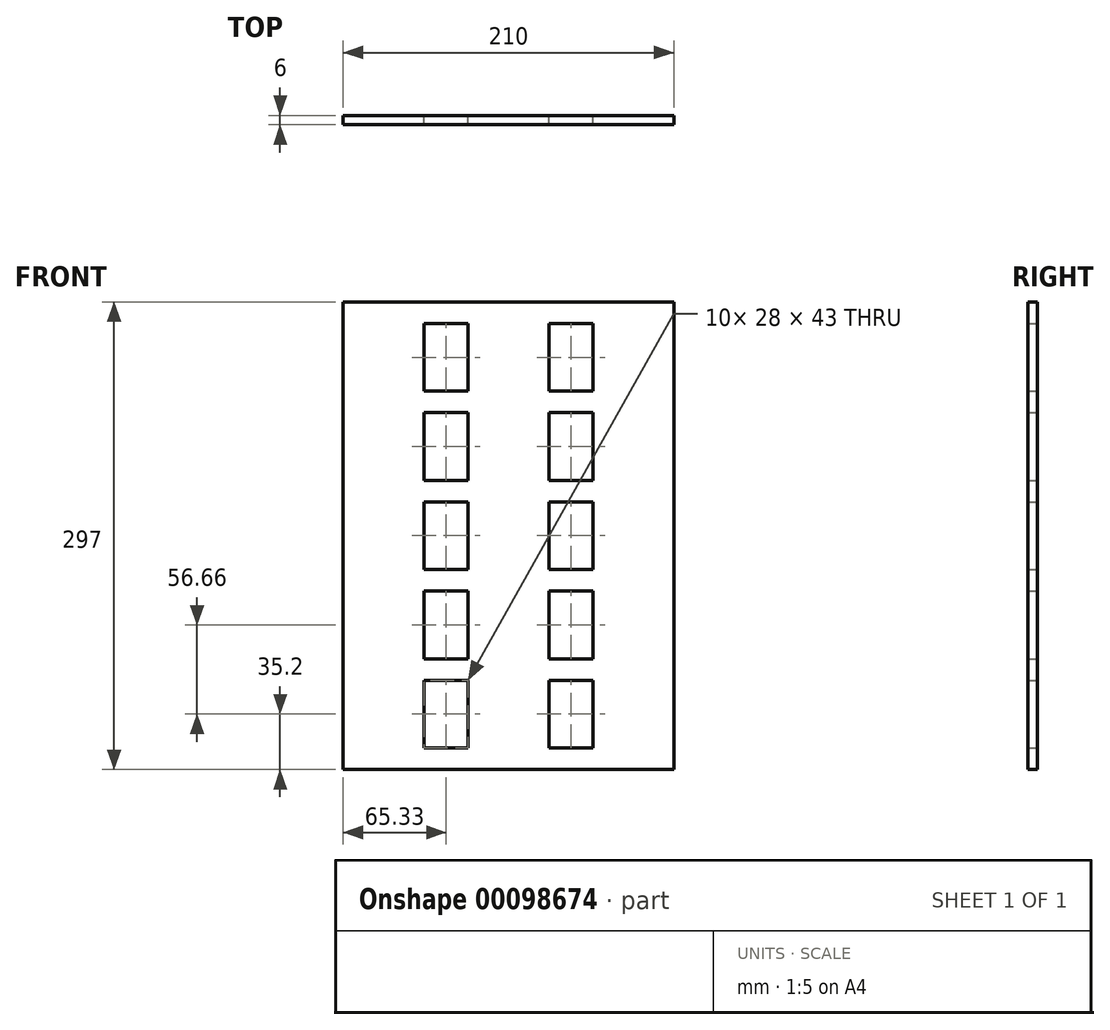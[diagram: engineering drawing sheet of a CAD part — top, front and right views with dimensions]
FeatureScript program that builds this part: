
annotation { "Feature Type Name" : "Feature", "Feature Type Description" : "" }
export const myFeature = defineFeature(function(context is Context, id is Id, definition is map)
    precondition{}
    {
        {
            var Q0;
            Q0=qCreatedBy(makeId("Front.planeOp"),FACE);
            var sketch = newSketch(context, id + "F0", { "sketchPlane" : qUnion([Q0])});
            skLineSegment(sketch, "E0.bottom", {"start": v(105, -148.5) * mm, "end": v(-105, -148.5) * mm});
            skLineSegment(sketch, "E0.top", {"start": v(105, 148.5) * mm, "end": v(-105, 148.5) * mm});
            skLineSegment(sketch, "E0.left", {"start": v(105, -148.5) * mm, "end": v(105, 148.5) * mm});
            skLineSegment(sketch, "E0.right", {"start": v(-105, -148.5) * mm, "end": v(-105, 148.5) * mm});
            skLineSegment(sketch, "E1.bottom", {"start": v(-25.67, 91.84) * mm, "end": v(-53.67, 91.84) * mm});
            skLineSegment(sketch, "E1.top", {"start": v(-25.67, 134.84) * mm, "end": v(-53.67, 134.84) * mm});
            skLineSegment(sketch, "E1.left", {"start": v(-25.67, 91.84) * mm, "end": v(-25.67, 134.84) * mm});
            skLineSegment(sketch, "E1.right", {"start": v(-53.67, 91.84) * mm, "end": v(-53.67, 134.84) * mm});
            skPoint(sketch, "E1.middle", {"position": v(-39.67, 113.34) * mm});
            skLineSegment(sketch, "E2.0.1.0", {"start": v(-25.67, 78.18) * mm, "end": v(-53.67, 78.18) * mm});
            skLineSegment(sketch, "E2.0.1.1", {"start": v(-53.67, 35.18) * mm, "end": v(-53.67, 78.18) * mm});
            skLineSegment(sketch, "E2.0.1.2", {"start": v(-25.67, 35.18) * mm, "end": v(-53.67, 35.18) * mm});
            skLineSegment(sketch, "E2.0.1.3", {"start": v(-25.67, 35.18) * mm, "end": v(-25.67, 78.18) * mm});
            skLineSegment(sketch, "E2.0.2.0", {"start": v(-25.67, 21.52) * mm, "end": v(-53.67, 21.52) * mm});
            skLineSegment(sketch, "E2.0.2.1", {"start": v(-53.67, -21.48) * mm, "end": v(-53.67, 21.52) * mm});
            skLineSegment(sketch, "E2.0.2.2", {"start": v(-25.67, -21.48) * mm, "end": v(-53.67, -21.48) * mm});
            skLineSegment(sketch, "E2.0.2.3", {"start": v(-25.67, -21.48) * mm, "end": v(-25.67, 21.52) * mm});
            skLineSegment(sketch, "E2.0.3.0", {"start": v(-25.67, -35.14) * mm, "end": v(-53.67, -35.14) * mm});
            skLineSegment(sketch, "E2.0.3.1", {"start": v(-53.67, -78.14) * mm, "end": v(-53.67, -35.14) * mm});
            skLineSegment(sketch, "E2.0.3.2", {"start": v(-25.67, -78.14) * mm, "end": v(-53.67, -78.14) * mm});
            skLineSegment(sketch, "E2.0.3.3", {"start": v(-25.67, -78.14) * mm, "end": v(-25.67, -35.14) * mm});
            skLineSegment(sketch, "E2.0.4.0", {"start": v(-25.67, -91.8) * mm, "end": v(-53.67, -91.8) * mm});
            skLineSegment(sketch, "E2.0.4.1", {"start": v(-53.67, -134.8) * mm, "end": v(-53.67, -91.8) * mm});
            skLineSegment(sketch, "E2.0.4.2", {"start": v(-25.67, -134.8) * mm, "end": v(-53.67, -134.8) * mm});
            skLineSegment(sketch, "E2.0.4.3", {"start": v(-25.67, -134.8) * mm, "end": v(-25.67, -91.8) * mm});
            skLineSegment(sketch, "E2.1.0.0", {"start": v(53.66, 134.84) * mm, "end": v(25.66, 134.84) * mm});
            skLineSegment(sketch, "E2.1.0.1", {"start": v(25.66, 91.84) * mm, "end": v(25.66, 134.84) * mm});
            skLineSegment(sketch, "E2.1.0.2", {"start": v(53.66, 91.84) * mm, "end": v(25.66, 91.84) * mm});
            skLineSegment(sketch, "E2.1.0.3", {"start": v(53.66, 91.84) * mm, "end": v(53.66, 134.84) * mm});
            skLineSegment(sketch, "E2.1.1.0", {"start": v(53.66, 78.18) * mm, "end": v(25.66, 78.18) * mm});
            skLineSegment(sketch, "E2.1.1.1", {"start": v(25.66, 35.18) * mm, "end": v(25.66, 78.18) * mm});
            skLineSegment(sketch, "E2.1.1.2", {"start": v(53.66, 35.18) * mm, "end": v(25.66, 35.18) * mm});
            skLineSegment(sketch, "E2.1.1.3", {"start": v(53.66, 35.18) * mm, "end": v(53.66, 78.18) * mm});
            skLineSegment(sketch, "E2.1.2.0", {"start": v(53.66, 21.52) * mm, "end": v(25.66, 21.52) * mm});
            skLineSegment(sketch, "E2.1.2.1", {"start": v(25.66, -21.48) * mm, "end": v(25.66, 21.52) * mm});
            skLineSegment(sketch, "E2.1.2.2", {"start": v(53.66, -21.48) * mm, "end": v(25.66, -21.48) * mm});
            skLineSegment(sketch, "E2.1.2.3", {"start": v(53.66, -21.48) * mm, "end": v(53.66, 21.52) * mm});
            skLineSegment(sketch, "E2.1.3.0", {"start": v(53.66, -35.14) * mm, "end": v(25.66, -35.14) * mm});
            skLineSegment(sketch, "E2.1.3.1", {"start": v(25.66, -78.14) * mm, "end": v(25.66, -35.14) * mm});
            skLineSegment(sketch, "E2.1.3.2", {"start": v(53.66, -78.14) * mm, "end": v(25.66, -78.14) * mm});
            skLineSegment(sketch, "E2.1.3.3", {"start": v(53.66, -78.14) * mm, "end": v(53.66, -35.14) * mm});
            skLineSegment(sketch, "E2.1.4.0", {"start": v(53.66, -91.8) * mm, "end": v(25.66, -91.8) * mm});
            skLineSegment(sketch, "E2.1.4.1", {"start": v(25.66, -134.8) * mm, "end": v(25.66, -91.8) * mm});
            skLineSegment(sketch, "E2.1.4.2", {"start": v(53.66, -134.8) * mm, "end": v(25.66, -134.8) * mm});
            skLineSegment(sketch, "E2.1.4.3", {"start": v(53.66, -134.8) * mm, "end": v(53.66, -91.8) * mm});
            skLineSegment(sketch, "E2.direction1", {"start": v(-53.67, 134.84) * mm, "end": v(25.66, 134.84) * mm, "construction": true});
            skLineSegment(sketch, "E2.direction2", {"start": v(-53.67, 134.84) * mm, "end": v(-53.67, 78.18) * mm, "construction": true});
            skSolve(sketch);
        }
        {
            var Q0;
            Q0 = qSketchRegion(id + "F0", true);
            extrude(context, id + "F1", {"entities" : qUnion([Q0]), "depth" : 6 * mm});
        }
    });
